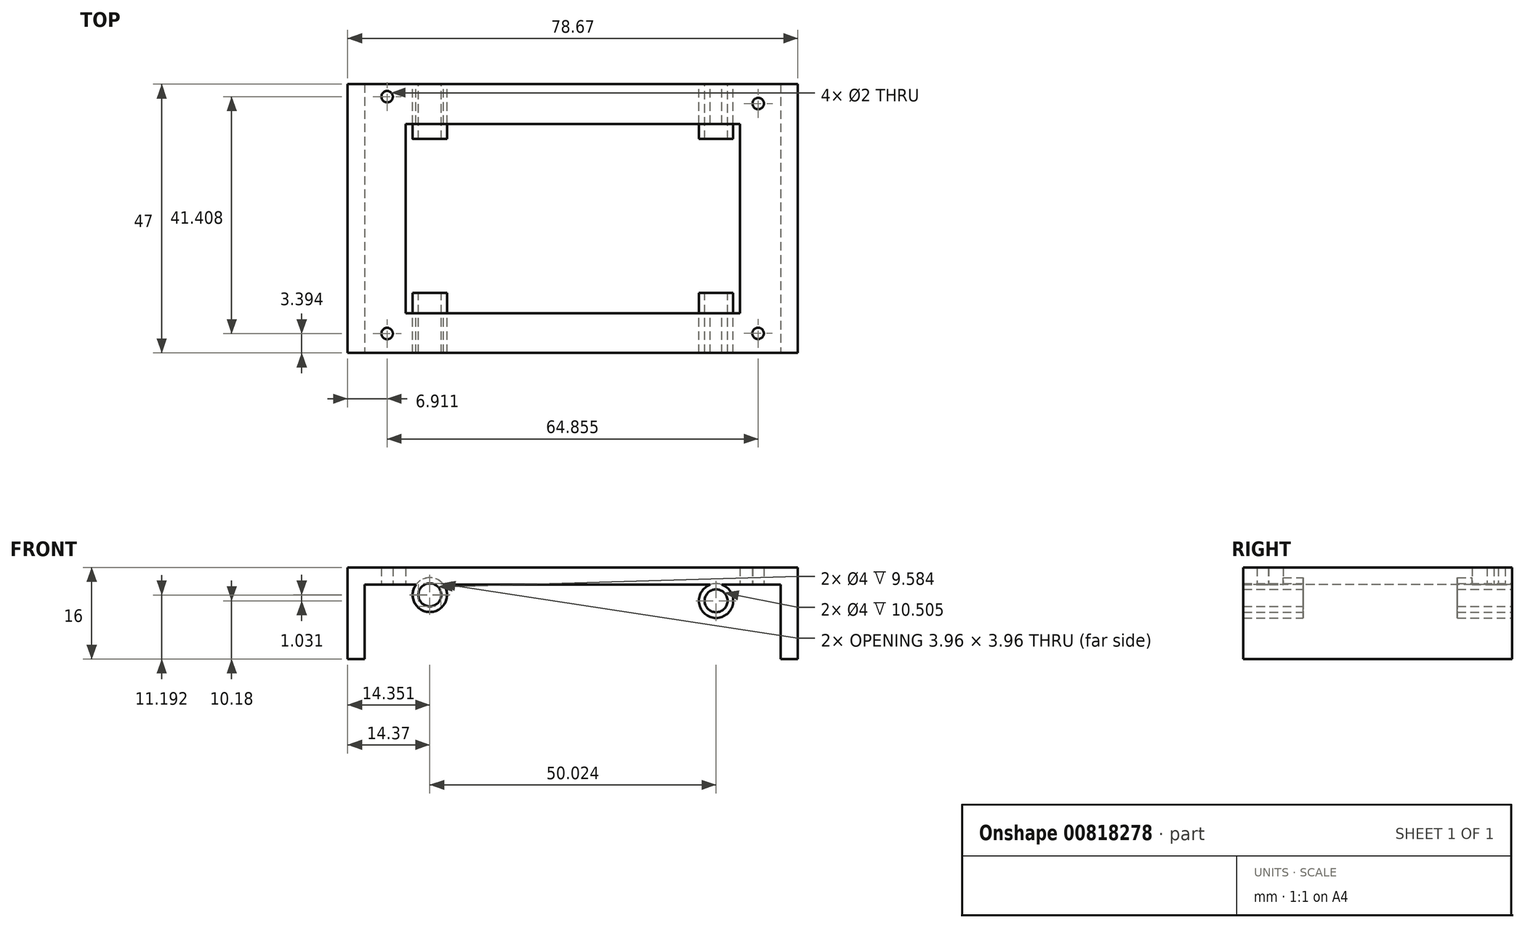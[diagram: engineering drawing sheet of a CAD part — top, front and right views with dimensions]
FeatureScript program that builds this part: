
annotation { "Feature Type Name" : "Feature", "Feature Type Description" : "" }
export const myFeature = defineFeature(function(context is Context, id is Id, definition is map)
    precondition{}
    {
        {
            var Q0;
            Q0=qCreatedBy(makeId("Top.planeOp"),FACE);
            var sketch = newSketch(context, id + "F0", { "sketchPlane" : qUnion([Q0])});
            skLineSegment(sketch, "E0.bottom", {"start": v(-45.34, 30.12) * mm, "end": v(33.66, 30.12) * mm});
            skLineSegment(sketch, "E0.top", {"start": v(-45.34, -16.88) * mm, "end": v(33.66, -16.88) * mm});
            skLineSegment(sketch, "E0.left", {"start": v(-45.34, 30.12) * mm, "end": v(-45.34, -16.88) * mm});
            skLineSegment(sketch, "E0.right", {"start": v(33.66, 30.12) * mm, "end": v(33.66, -16.88) * mm});
            skLineSegment(sketch, "E1.bottom", {"start": v(-42.34, 30.12) * mm, "end": v(30.33, 30.12) * mm});
            skLineSegment(sketch, "E1.top", {"start": v(-42.34, -16.88) * mm, "end": v(30.33, -16.88) * mm});
            skLineSegment(sketch, "E1.left", {"start": v(-42.34, 30.12) * mm, "end": v(-42.34, -16.88) * mm});
            skLineSegment(sketch, "E1.right", {"start": v(30.33, 30.12) * mm, "end": v(30.33, -16.88) * mm});
            skPoint(sketch, "E1.middle", {"position": v(-6, 6.62) * mm});
            skLineSegment(sketch, "E2.bottom", {"start": v(-35.22, 23.15) * mm, "end": v(23.21, 23.15) * mm});
            skLineSegment(sketch, "E2.top", {"start": v(-35.22, -9.91) * mm, "end": v(23.21, -9.91) * mm});
            skLineSegment(sketch, "E2.left", {"start": v(-35.22, 23.15) * mm, "end": v(-35.22, -9.91) * mm});
            skLineSegment(sketch, "E2.right", {"start": v(23.21, 23.15) * mm, "end": v(23.21, -9.91) * mm});
            skCircle(sketch, "E3", {"center": v(26.43, 26.73) * mm, "radius": 1 * mm});
            skCircle(sketch, "E4", {"center": v(26.4, -13.46) * mm, "radius": 1 * mm});
            skCircle(sketch, "E5", {"center": v(-38.43, -13.49) * mm, "radius": 1 * mm});
            skCircle(sketch, "E6", {"center": v(-38.43, 27.92) * mm, "radius": 1 * mm});
            skSolve(sketch);
        }
        {
            var Q0;
            {var subQ0=sQuery(id+"F0.wireOp",EDGE,"E1.left");Q0=makeQuery(id+"F0.imprint","IMPRINT",FACE,{"disambiguationData":[TD([[makeQuery(id+"F0.imprint","IMPRINT",EDGE,{"derivedFrom":subQ0}),1.0]])]});}
            var Q1;
            {var subQ0=sQuery(id+"F0.wireOp",EDGE,"E1.left");Q1=makeQuery(id+"F0.imprint","IMPRINT",FACE,{"disambiguationData":[TD([[makeQuery(id+"F0.imprint","IMPRINT",EDGE,{"derivedFrom":subQ0}),1.0]])]});}
            extrude(context, id + "F1", {"entities" : qUnion([Q0, Q1]), "depth" : 3 * mm, "offsetDistance" : 25 * mm});
        }
        {
            var Q0;
            Q0=makeQuery(id+"F1.opExtrude","CAP_FACE",FACE,{"disambiguationData":[OSD([sQuery(id+"F0.wireOp",EDGE,"E0.bottom"),sQuery(id+"F0.wireOp",EDGE,"E0.top"),sQuery(id+"F0.wireOp",EDGE,"E1.left"),sQuery(id+"F0.wireOp",EDGE,"E1.right"),sQuery(id+"F0.wireOp",EDGE,"E2.bottom"),sQuery(id+"F0.wireOp",EDGE,"E2.top"),sQuery(id+"F0.wireOp",EDGE,"E2.left"),sQuery(id+"F0.wireOp",EDGE,"E2.right"),sQuery(id+"F0.wireOp",EDGE,"E3"),sQuery(id+"F0.wireOp",EDGE,"E4"),sQuery(id+"F0.wireOp",EDGE,"E5"),sQuery(id+"F0.wireOp",EDGE,"E6")])],"isStart":false});
            var sketch = newSketch(context, id + "F2", { "sketchPlane" : qUnion([Q0])});
            skLineSegment(sketch, "E7.bottom", {"start": v(-42.34, -16.88) * mm, "end": v(-45.34, -16.88) * mm});
            skLineSegment(sketch, "E7.top", {"start": v(-42.34, 30.12) * mm, "end": v(-45.34, 30.12) * mm});
            skLineSegment(sketch, "E7.left", {"start": v(-42.34, -16.88) * mm, "end": v(-42.34, 30.12) * mm});
            skLineSegment(sketch, "E7.right", {"start": v(-45.34, -16.88) * mm, "end": v(-45.34, 30.12) * mm});
            skLineSegment(sketch, "E8.bottom", {"start": v(30.33, -16.88) * mm, "end": v(33.33, -16.88) * mm});
            skLineSegment(sketch, "E8.top", {"start": v(30.33, 30.12) * mm, "end": v(33.33, 30.12) * mm});
            skLineSegment(sketch, "E8.left", {"start": v(30.33, -16.88) * mm, "end": v(30.33, 30.12) * mm});
            skLineSegment(sketch, "E8.right", {"start": v(33.33, -16.88) * mm, "end": v(33.33, 30.12) * mm});
            skSolve(sketch);
        }
        {
            var Q0;
            Q0=makeQuery(id+"F2.imprint","IMPRINT",FACE,{"disambiguationData":[TD([[makeQuery(id+"F2.imprint","IMPRINT",EDGE,{"derivedFrom":sQuery(id+"F2.wireOp",EDGE,"E8.bottom")}),1.0]])]});
            var Q1;
            Q1=makeQuery(id+"F2.imprint","IMPRINT",FACE,{"disambiguationData":[TD([[makeQuery(id+"F2.imprint","IMPRINT",EDGE,{"derivedFrom":sQuery(id+"F2.wireOp",EDGE,"E7.bottom")}),-1.0]])]});
            extrude(context, id + "F3", {"entities" : qUnion([Q0, Q1]), "operationType" : NewBodyOperationType.ADD, "oppositeDirection" : true, "depth" : 16 * mm, "offsetDistance" : 25 * mm});
        }
        {
            var Q0;
            Q0=makeQuery(id+"F3.boolean.opBoolean","MERGE",FACE,{"derivedFrom":[makeQuery(id+"F1.opExtrude","SWEPT_FACE",FACE,{"disambiguationData":[OSD([sQuery(id+"F0.wireOp",EDGE,"E0.bottom")])]}),makeQuery(id+"F3.opExtrude","SWEPT_FACE",FACE,{"disambiguationData":[OSD([sQuery(id+"F2.wireOp",EDGE,"E7.top")])]}),makeQuery(id+"F3.opExtrude","SWEPT_FACE",FACE,{"disambiguationData":[OSD([sQuery(id+"F2.wireOp",EDGE,"E8.top")])]})]});
            var sketch = newSketch(context, id + "F4", { "sketchPlane" : qUnion([Q0])});
            skCircle(sketch, "E9", {"center": v(-19.05, -2.82) * mm, "radius": 3 * mm});
            skPoint(sketch, "E9.first.point", {"position": v(-20.08, 0) * mm});
            skPoint(sketch, "E9.second.point", {"position": v(-21.94, -3.64) * mm});
            skPoint(sketch, "E9.third.point", {"position": v(-18.03, 0) * mm});
            skCircle(sketch, "E10", {"center": v(30.97, -1.79) * mm, "radius": 3 * mm});
            skPoint(sketch, "E10.first.point", {"position": v(28.56, 0) * mm});
            skPoint(sketch, "E10.second.point", {"position": v(33.38, -3.58) * mm});
            skPoint(sketch, "E10.third.point", {"position": v(33.38, 0) * mm});
            skSolve(sketch);
        }
        {
            var Q0;
            Q0 = qSketchRegion(id + "F4", true);
            extrude(context, id + "F5", {"entities" : qUnion([Q0]), "operationType" : NewBodyOperationType.ADD, "oppositeDirection" : true, "depth" : 47 * mm, "offsetDistance" : 25 * mm});
        }
        {
            var Q0;
            Q0=makeQuery(id+"F5.boolean.opBoolean","MERGE",FACE,{"derivedFrom":[makeQuery(id+"F3.boolean.opBoolean","MERGE",FACE,{"derivedFrom":[makeQuery(id+"F1.opExtrude","SWEPT_FACE",FACE,{"disambiguationData":[OSD([sQuery(id+"F0.wireOp",EDGE,"E0.bottom")])]}),makeQuery(id+"F3.opExtrude","SWEPT_FACE",FACE,{"disambiguationData":[OSD([sQuery(id+"F2.wireOp",EDGE,"E7.top")])]}),makeQuery(id+"F3.opExtrude","SWEPT_FACE",FACE,{"disambiguationData":[OSD([sQuery(id+"F2.wireOp",EDGE,"E8.top")])]})]}),makeQuery(id+"F5.opExtrude","CAP_FACE",FACE,{"disambiguationData":[OSD([sQuery(id+"F4.wireOp",EDGE,"E9")])],"isStart":true}),makeQuery(id+"F5.opExtrude","CAP_FACE",FACE,{"disambiguationData":[OSD([sQuery(id+"F4.wireOp",EDGE,"E10")])],"isStart":true})]});
            var sketch = newSketch(context, id + "F6", { "sketchPlane" : qUnion([Q0])});
            skCircle(sketch, "E11", {"center": v(-19.05, -2.82) * mm, "radius": 2 * mm});
            skCircle(sketch, "E12", {"center": v(30.97, -1.79) * mm, "radius": 2 * mm});
            skSolve(sketch);
        }
        {
            var Q0;
            Q0=makeQuery(id+"F6.imprint","IMPRINT",FACE,{"disambiguationData":[TD([[makeQuery(id+"F6.imprint","IMPRINT",EDGE,{"derivedFrom":sQuery(id+"F6.wireOp",EDGE,"E12")}),1.0]])]});
            var Q1;
            Q1=makeQuery(id+"F6.imprint","IMPRINT",FACE,{"disambiguationData":[TD([[makeQuery(id+"F6.imprint","IMPRINT",EDGE,{"derivedFrom":sQuery(id+"F6.wireOp",EDGE,"E11")}),1.0]])]});
            extrude(context, id + "F7", {"entities" : qUnion([Q0, Q1]), "operationType" : NewBodyOperationType.REMOVE, "oppositeDirection" : true, "depth" : 59 * mm, "offsetDistance" : 25 * mm});
        }
        {
            var Q0;
            Q0=makeQuery(id+"F3.boolean.opBoolean","MERGE",FACE,{"derivedFrom":[makeQuery(id+"F1.opExtrude","CAP_FACE",FACE,{"disambiguationData":[OSD([sQuery(id+"F0.wireOp",EDGE,"E0.bottom"),sQuery(id+"F0.wireOp",EDGE,"E0.top"),sQuery(id+"F0.wireOp",EDGE,"E1.left"),sQuery(id+"F0.wireOp",EDGE,"E1.right"),sQuery(id+"F0.wireOp",EDGE,"E2.bottom"),sQuery(id+"F0.wireOp",EDGE,"E2.top"),sQuery(id+"F0.wireOp",EDGE,"E2.left"),sQuery(id+"F0.wireOp",EDGE,"E2.right"),sQuery(id+"F0.wireOp",EDGE,"E3"),sQuery(id+"F0.wireOp",EDGE,"E4"),sQuery(id+"F0.wireOp",EDGE,"E5"),sQuery(id+"F0.wireOp",EDGE,"E6")])],"isStart":false}),makeQuery(id+"F3.opExtrude","CAP_FACE",FACE,{"disambiguationData":[OSD([sQuery(id+"F2.wireOp",EDGE,"E7.bottom"),sQuery(id+"F2.wireOp",EDGE,"E7.top"),sQuery(id+"F2.wireOp",EDGE,"E7.left"),sQuery(id+"F2.wireOp",EDGE,"E7.right")])],"isStart":true}),makeQuery(id+"F3.opExtrude","CAP_FACE",FACE,{"disambiguationData":[OSD([sQuery(id+"F2.wireOp",EDGE,"E8.bottom"),sQuery(id+"F2.wireOp",EDGE,"E8.top"),sQuery(id+"F2.wireOp",EDGE,"E8.left"),sQuery(id+"F2.wireOp",EDGE,"E8.right")])],"isStart":true})]});
            var sketch = newSketch(context, id + "F8", { "sketchPlane" : qUnion([Q0])});
            skLineSegment(sketch, "E13.bottom", {"start": v(-35.22, 20.54) * mm, "end": v(23.21, 20.54) * mm});
            skLineSegment(sketch, "E13.top", {"start": v(-35.22, -6.37) * mm, "end": v(23.21, -6.37) * mm});
            skLineSegment(sketch, "E13.left", {"start": v(-35.22, 20.54) * mm, "end": v(-35.22, -6.37) * mm});
            skLineSegment(sketch, "E13.right", {"start": v(23.21, 20.54) * mm, "end": v(23.21, -6.37) * mm});
            skSolve(sketch);
        }
        {
            var Q0;
            Q0=makeQuery(id+"F8.imprint","IMPRINT",FACE,{"disambiguationData":[TD([[makeQuery(id+"F8.imprint","IMPRINT",EDGE,{"derivedFrom":sQuery(id+"F8.wireOp",EDGE,"E13.bottom")}),-1.0]])]});
            extrude(context, id + "F9", {"entities" : qUnion([Q0]), "operationType" : NewBodyOperationType.REMOVE, "oppositeDirection" : true, "depth" : 25 * mm, "offsetDistance" : 25 * mm});
        }
    });
